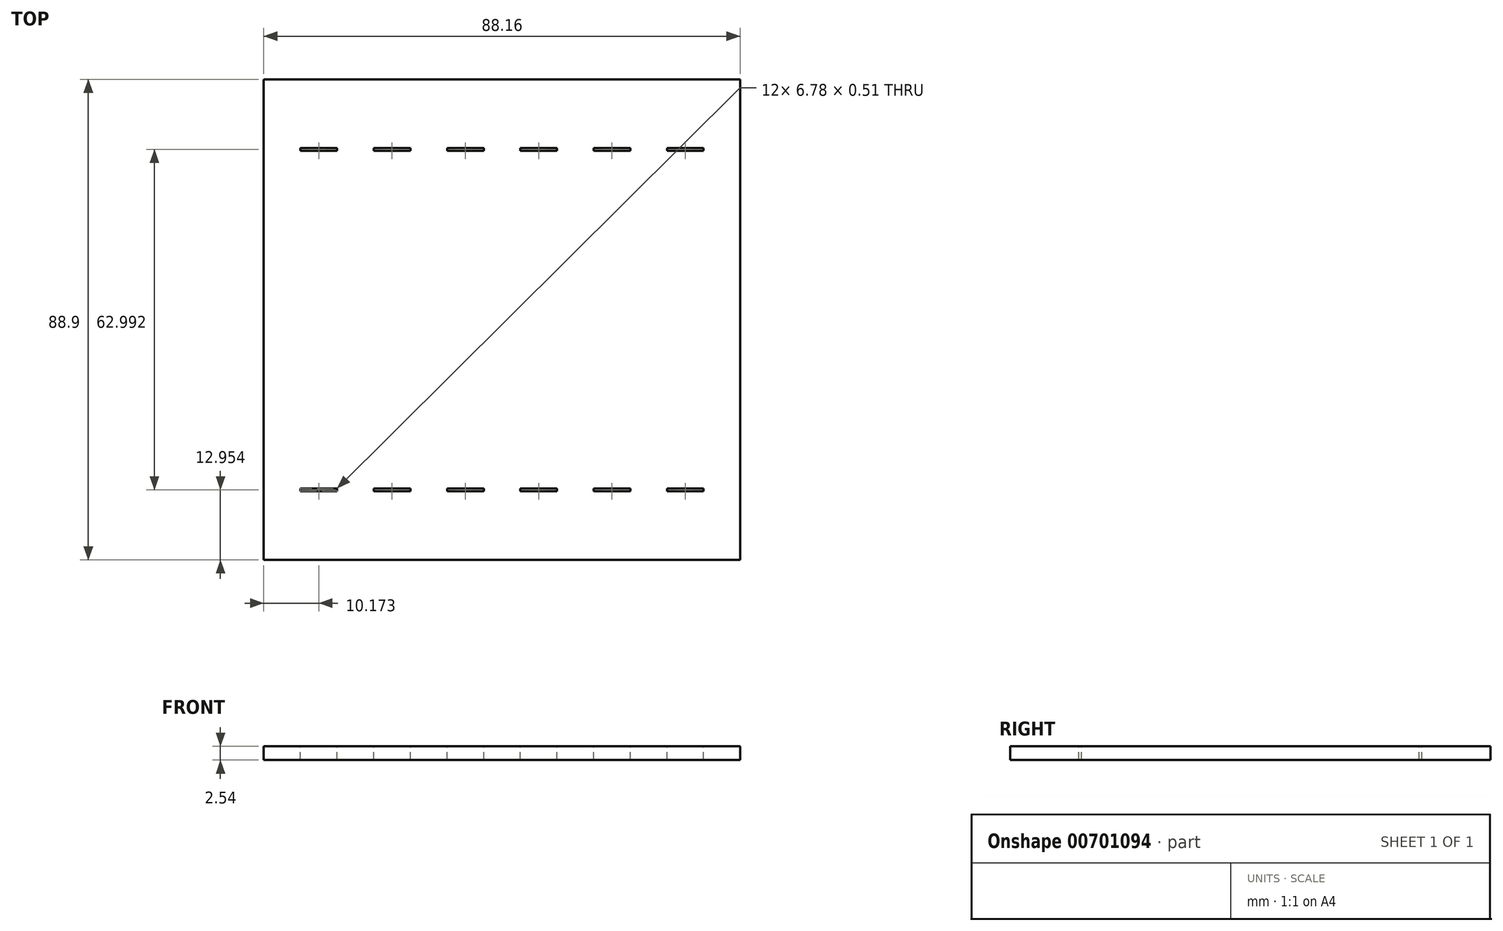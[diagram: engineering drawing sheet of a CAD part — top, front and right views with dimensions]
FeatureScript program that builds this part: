
annotation { "Feature Type Name" : "Feature", "Feature Type Description" : "" }
export const myFeature = defineFeature(function(context is Context, id is Id, definition is map)
    precondition{}
    {
        {
            var Q0;
            Q0=qCreatedBy(makeId("Top.planeOp"),FACE);
            var sketch = newSketch(context, id + "F0", { "sketchPlane" : qUnion([Q0])});
            skLineSegment(sketch, "E0.bottom", {"start": v(0, 0) * mm, "end": v(88.16, 0) * mm});
            skLineSegment(sketch, "E0.top", {"start": v(0, -88.9) * mm, "end": v(88.16, -88.9) * mm});
            skLineSegment(sketch, "E0.left", {"start": v(0, 0) * mm, "end": v(0, -88.9) * mm});
            skLineSegment(sketch, "E0.right", {"start": v(88.16, 0) * mm, "end": v(88.16, -88.9) * mm});
            skLineSegment(sketch, "E1.bottom", {"start": v(6.78, -12.7) * mm, "end": v(13.56, -12.7) * mm});
            skLineSegment(sketch, "E1.top", {"start": v(6.78, -13.2) * mm, "end": v(13.56, -13.2) * mm});
            skLineSegment(sketch, "E1.left", {"start": v(6.78, -12.7) * mm, "end": v(6.78, -13.2) * mm});
            skLineSegment(sketch, "E1.right", {"start": v(13.56, -12.7) * mm, "end": v(13.56, -13.2) * mm});
            skLineSegment(sketch, "E2", {"start": v(16.95, 0) * mm, "end": v(16.95, -88.9) * mm, "construction": true});
            skLineSegment(sketch, "E3.MirrorCS", {"start": v(27.13, -12.7) * mm, "end": v(20.35, -12.7) * mm});
            skLineSegment(sketch, "E4.MirrorCS", {"start": v(27.13, -13.2) * mm, "end": v(20.35, -13.2) * mm});
            skLineSegment(sketch, "E5.MirrorCS", {"start": v(20.35, -12.7) * mm, "end": v(20.35, -13.2) * mm});
            skLineSegment(sketch, "E6.MirrorCS", {"start": v(27.13, -12.7) * mm, "end": v(27.13, -13.2) * mm});
            skLineSegment(sketch, "E7", {"start": v(30.53, 0) * mm, "end": v(30.53, -88.9) * mm, "construction": true});
            skLineSegment(sketch, "E8.MirrorCS", {"start": v(33.93, -12.7) * mm, "end": v(33.93, -13.2) * mm});
            skLineSegment(sketch, "E9.MirrorCS", {"start": v(40.72, -12.7) * mm, "end": v(40.72, -13.2) * mm});
            skLineSegment(sketch, "E10.MirrorCS", {"start": v(33.93, -13.2) * mm, "end": v(40.72, -13.2) * mm});
            skLineSegment(sketch, "E11.MirrorCS", {"start": v(33.93, -12.7) * mm, "end": v(40.72, -12.7) * mm});
            skLineSegment(sketch, "E12.MirrorCS", {"start": v(54.28, -12.7) * mm, "end": v(54.28, -13.2) * mm});
            skLineSegment(sketch, "E13.MirrorCS", {"start": v(47.5, -12.7) * mm, "end": v(47.5, -13.2) * mm});
            skLineSegment(sketch, "E14.MirrorCS", {"start": v(54.28, -13.2) * mm, "end": v(47.5, -13.2) * mm});
            skLineSegment(sketch, "E15.MirrorCS", {"start": v(54.28, -12.7) * mm, "end": v(47.5, -12.7) * mm});
            skLineSegment(sketch, "E16", {"start": v(57.67, 0) * mm, "end": v(57.67, -88.9) * mm, "construction": true});
            skLineSegment(sketch, "E17.MirrorCS", {"start": v(61.06, -12.7) * mm, "end": v(61.06, -13.2) * mm});
            skLineSegment(sketch, "E18.MirrorCS", {"start": v(67.84, -12.7) * mm, "end": v(67.84, -13.2) * mm});
            skLineSegment(sketch, "E19.MirrorCS", {"start": v(61.06, -13.2) * mm, "end": v(67.84, -13.2) * mm});
            skLineSegment(sketch, "E20.MirrorCS", {"start": v(61.06, -12.7) * mm, "end": v(67.84, -12.7) * mm});
            skLineSegment(sketch, "E21.MirrorCS", {"start": v(74.63, -12.7) * mm, "end": v(74.63, -13.2) * mm});
            skLineSegment(sketch, "E22.MirrorCS", {"start": v(81.4, -12.7) * mm, "end": v(81.4, -13.2) * mm});
            skLineSegment(sketch, "E23.MirrorCS", {"start": v(81.4, -13.2) * mm, "end": v(74.63, -13.2) * mm});
            skLineSegment(sketch, "E24.MirrorCS", {"start": v(81.4, -12.7) * mm, "end": v(74.63, -12.7) * mm});
            skLineSegment(sketch, "E25", {"start": v(0, -44.45) * mm, "end": v(88.16, -44.45) * mm, "construction": true});
            skLineSegment(sketch, "E26.MirrorCS", {"start": v(13.56, -76.2) * mm, "end": v(13.56, -75.7) * mm});
            skLineSegment(sketch, "E27.MirrorCS", {"start": v(20.35, -76.2) * mm, "end": v(20.35, -75.7) * mm});
            skLineSegment(sketch, "E28.MirrorCS", {"start": v(27.13, -76.2) * mm, "end": v(27.13, -75.7) * mm});
            skLineSegment(sketch, "E29.MirrorCS", {"start": v(74.63, -76.2) * mm, "end": v(74.63, -75.7) * mm});
            skLineSegment(sketch, "E30.MirrorCS", {"start": v(61.06, -76.2) * mm, "end": v(61.06, -75.7) * mm});
            skLineSegment(sketch, "E31.MirrorCS", {"start": v(6.78, -76.2) * mm, "end": v(6.78, -75.7) * mm});
            skLineSegment(sketch, "E32.MirrorCS", {"start": v(40.72, -76.2) * mm, "end": v(40.72, -75.7) * mm});
            skLineSegment(sketch, "E33.MirrorCS", {"start": v(33.93, -76.2) * mm, "end": v(33.93, -75.7) * mm});
            skLineSegment(sketch, "E34.MirrorCS", {"start": v(67.84, -76.2) * mm, "end": v(67.84, -75.7) * mm});
            skLineSegment(sketch, "E35.MirrorCS", {"start": v(47.5, -76.2) * mm, "end": v(47.5, -75.7) * mm});
            skLineSegment(sketch, "E36.MirrorCS", {"start": v(54.28, -76.2) * mm, "end": v(54.28, -75.7) * mm});
            skLineSegment(sketch, "E37.MirrorCS", {"start": v(81.4, -76.2) * mm, "end": v(81.4, -75.7) * mm});
            skLineSegment(sketch, "E38.MirrorCS", {"start": v(6.78, -76.2) * mm, "end": v(13.56, -76.2) * mm});
            skLineSegment(sketch, "E39.MirrorCS", {"start": v(6.78, -75.7) * mm, "end": v(13.56, -75.7) * mm});
            skLineSegment(sketch, "E40.MirrorCS", {"start": v(54.28, -76.2) * mm, "end": v(47.5, -76.2) * mm});
            skLineSegment(sketch, "E41.MirrorCS", {"start": v(81.4, -76.2) * mm, "end": v(74.63, -76.2) * mm});
            skLineSegment(sketch, "E42.MirrorCS", {"start": v(54.28, -75.7) * mm, "end": v(47.5, -75.7) * mm});
            skLineSegment(sketch, "E43.MirrorCS", {"start": v(33.93, -76.2) * mm, "end": v(40.72, -76.2) * mm});
            skLineSegment(sketch, "E44.MirrorCS", {"start": v(81.4, -75.7) * mm, "end": v(74.63, -75.7) * mm});
            skLineSegment(sketch, "E45.MirrorCS", {"start": v(33.93, -75.7) * mm, "end": v(40.72, -75.7) * mm});
            skLineSegment(sketch, "E46.MirrorCS", {"start": v(27.13, -75.7) * mm, "end": v(20.35, -75.7) * mm});
            skLineSegment(sketch, "E47.MirrorCS", {"start": v(27.13, -76.2) * mm, "end": v(20.35, -76.2) * mm});
            skLineSegment(sketch, "E48.MirrorCS", {"start": v(61.06, -75.7) * mm, "end": v(67.84, -75.7) * mm});
            skLineSegment(sketch, "E49.MirrorCS", {"start": v(61.06, -76.2) * mm, "end": v(67.84, -76.2) * mm});
            skSolve(sketch);
        }
        {
            var Q0;
            Q0=makeQuery(id+"F0.imprint","IMPRINT",FACE,{"disambiguationData":[TD([[makeQuery(id+"F0.imprint","IMPRINT",EDGE,{"derivedFrom":sQuery(id+"F0.wireOp",EDGE,"E0.bottom")}),-1.0]])]});
            extrude(context, id + "F1", {"entities" : qUnion([Q0]), "oppositeDirection" : true, "depth" : 2.54 * mm, "offsetDistance" : 25.4 * mm});
        }
    });
